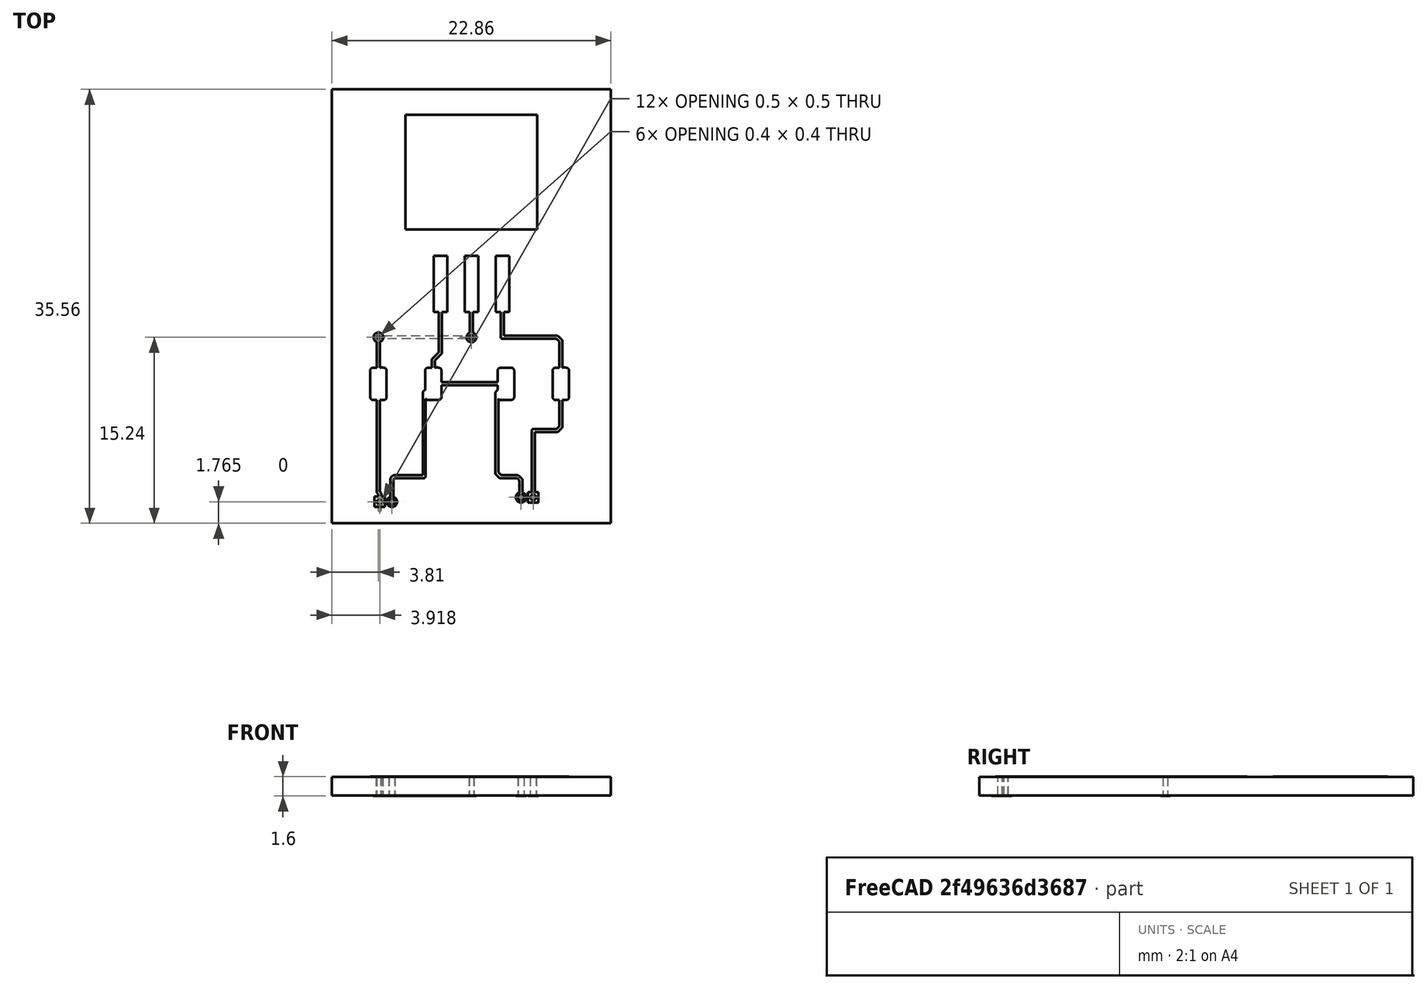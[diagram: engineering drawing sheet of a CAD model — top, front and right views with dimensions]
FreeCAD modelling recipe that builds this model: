
FCSTD DOCUMENT  (FreeCAD 0.18R15221 (Git))
Label: copper
License: All rights reserved
LicenseURL: http://en.wikipedia.org/wiki/All_rights_reserved
objects: Path::FeatureArea×19, Part::Feature×15, Part::Extrusion×5, Part::MultiFuse×1, Part::Cut×1
note: 60 computed .brp shape members not serialized (recipe doc carries the construction recipe); baked Part::Feature solids carry a one-line shape summary decoded from their .brp

FEATURE [Part::Feature] holes_wire  label="holes_wire#F.Cu#0"
  shape: bbox 13.13 x 13.93 x 2e-07 mm, 0 faces, 0 solids (baked)
FEATURE [Part::Feature] board_wire  label="board_wire#F.Cu"
  shape: bbox 22.86 x 35.56 x 2e-07 mm, 0 faces, 0 solids (baked)
FEATURE [Path::FeatureArea] board_area  label="board_area#F.Cu"
  Accuracy = 0.01
  Angle = 45
  AngleShift = 0
  CleanDistance = 0
  ClipFill = 0
  ClipperScale = 10000000
  Coplanar = 0
  Deflection = 0.01
  EndType = 0
  Explode = false
  ExtraPass = 0
  Fill = 1
  FitArcs = false
  FromCenter = false
  JoinType = 0
  LastStepover = 0
  MaxArcPoints = 100
  MinArcPoints = 4
  MiterLimit = 2
  OpenMode = 0
  Operation = 0
  Outline = false
  PocketExtraOffset = 0
  PocketLastStepover = 0
  PocketMode = 0
  PocketStepover = 0
  Project = false
  Reorient = false
  RoundPrecision = 0
  SectionCount = 0
  SectionMode = 2
  SectionOffset = 0
  SectionTolerance = 1e-06
  Shift = 0
  Simplify = false
  Sources = -> [board_wire]
  Stepdown = 1
  Stepover = 0
  SubjectFill = 0
  Thicken = false
  Tolerance = 1e-07
  ToolRadius = 1
  Unit = 1
FEATURE [Path::FeatureArea] board_area001  label="board_area001#F.Cu"
  Accuracy = 0.01
  Angle = 45
  AngleShift = 0
  CleanDistance = 0
  ClipFill = 0
  ClipperScale = 10000000
  Coplanar = 0
  Deflection = 0.01
  EndType = 0
  Explode = false
  ExtraPass = 0
  Fill = 1
  FitArcs = true
  FromCenter = false
  JoinType = 0
  LastStepover = 0
  MaxArcPoints = 100
  MinArcPoints = 4
  MiterLimit = 2
  OpenMode = 0
  Operation = 1
  Outline = false
  PocketExtraOffset = 0
  PocketLastStepover = 0
  PocketMode = 0
  PocketStepover = 0
  Project = false
  Reorient = false
  RoundPrecision = 0
  SectionCount = 0
  SectionMode = 2
  SectionOffset = 0
  SectionTolerance = 1e-06
  Shift = 0
  Simplify = false
  Sources = -> [board_area,holes_wire]
  Stepdown = 1
  Stepover = 0
  SubjectFill = 0
  Thicken = false
  Tolerance = 1e-07
  ToolRadius = 1
  Unit = 1
FEATURE [Part::Extrusion] board_solid  label="board_solid#F.Cu"
  Base = -> board_area001
  Dir = (0,0,1.53)
  DirMode = 0
  FaceMakerClass = Part::FaceMakerBullseye
  LengthFwd = 0
  LengthRev = 0
  Solid = false
  Symmetric = false
FEATURE [Part::Feature] pads_wire  label="pads_wire#F.Cu#0#C2"
  shape: bbox 5.85 x 2.65 x 2e-07 mm, 0 faces, 0 solids (baked)
FEATURE [Path::FeatureArea] pads_area  label="pads_area#F.Cu#0#C2"
  Accuracy = 0.01
  Angle = 45
  AngleShift = 0
  CleanDistance = 0
  ClipFill = 0
  ClipperScale = 10000000
  Coplanar = 0
  Deflection = 0.01
  EndType = 0
  Explode = false
  ExtraPass = 0
  Fill = 1
  FitArcs = false
  FromCenter = false
  JoinType = 0
  LastStepover = 0
  MaxArcPoints = 100
  MinArcPoints = 4
  MiterLimit = 2
  OpenMode = 0
  Operation = 0
  Outline = false
  Placement = pos=(199.1,-80.01,0) rot=(0,0,1;0rad)
  PocketExtraOffset = 0
  PocketLastStepover = 0
  PocketMode = 0
  PocketStepover = 0
  Project = false
  Reorient = false
  RoundPrecision = 0
  SectionCount = 0
  SectionMode = 2
  SectionOffset = 0
  SectionTolerance = 1e-06
  Shift = 0
  Simplify = false
  Sources = -> [pads_wire]
  Stepdown = 1
  Stepover = 0
  SubjectFill = 0
  Thicken = false
  Tolerance = 1e-07
  ToolRadius = 1
  Unit = 1
FEATURE [Part::Feature] pads_wire001  label="pads_wire001#F.Cu#1#J2"
  shape: bbox 0.85 x 1.85 x 2e-07 mm, 0 faces, 0 solids (baked)
FEATURE [Path::FeatureArea] pads_area001  label="pads_area001#F.Cu#1#J2"
  Accuracy = 0.01
  Angle = 45
  AngleShift = 0
  CleanDistance = 0
  ClipFill = 0
  ClipperScale = 10000000
  Coplanar = 0
  Deflection = 0.01
  EndType = 0
  Explode = false
  ExtraPass = 0
  Fill = 1
  FitArcs = false
  FromCenter = false
  JoinType = 0
  LastStepover = 0
  MaxArcPoints = 100
  MinArcPoints = 4
  MiterLimit = 2
  OpenMode = 0
  Operation = 0
  Outline = false
  Placement = pos=(196.958,-89.6755,0) rot=(0,0,1;1.5708rad)
  PocketExtraOffset = 0
  PocketLastStepover = 0
  PocketMode = 0
  PocketStepover = 0
  Project = false
  Reorient = false
  RoundPrecision = 0
  SectionCount = 0
  SectionMode = 2
  SectionOffset = 0
  SectionTolerance = 1e-06
  Shift = 0
  Simplify = false
  Sources = -> [pads_wire001]
  Stepdown = 1
  Stepover = 0
  SubjectFill = 0
  Thicken = false
  Tolerance = 1e-07
  ToolRadius = 1
  Unit = 1
FEATURE [Part::Feature] pads_wire002  label="pads_wire002#F.Cu#2#J1"
  shape: bbox 0.85 x 1.85 x 2e-07 mm, 0 faces, 0 solids (baked)
FEATURE [Path::FeatureArea] pads_area002  label="pads_area002#F.Cu#2#J1"
  Accuracy = 0.01
  Angle = 45
  AngleShift = 0
  CleanDistance = 0
  ClipFill = 0
  ClipperScale = 10000000
  Coplanar = 0
  Deflection = 0.01
  EndType = 0
  Explode = false
  ExtraPass = 0
  Fill = 1
  FitArcs = false
  FromCenter = false
  JoinType = 0
  LastStepover = 0
  MaxArcPoints = 100
  MinArcPoints = 4
  MiterLimit = 2
  OpenMode = 0
  Operation = 0
  Outline = false
  Placement = pos=(209.534,-89.3136,0) rot=(0,0,1;4.71239rad)
  PocketExtraOffset = 0
  PocketLastStepover = 0
  PocketMode = 0
  PocketStepover = 0
  Project = false
  Reorient = false
  RoundPrecision = 0
  SectionCount = 0
  SectionMode = 2
  SectionOffset = 0
  SectionTolerance = 1e-06
  Shift = 0
  Simplify = false
  Sources = -> [pads_wire002]
  Stepdown = 1
  Stepover = 0
  SubjectFill = 0
  Thicken = false
  Tolerance = 1e-07
  ToolRadius = 1
  Unit = 1
FEATURE [Part::Feature] pads_wire003  label="pads_wire003#F.Cu#3#C1"
  shape: bbox 5.85 x 2.65 x 2e-07 mm, 0 faces, 0 solids (baked)
FEATURE [Path::FeatureArea] pads_area003  label="pads_area003#F.Cu#3#C1"
  Accuracy = 0.01
  Angle = 45
  AngleShift = 0
  CleanDistance = 0
  ClipFill = 0
  ClipperScale = 10000000
  Coplanar = 0
  Deflection = 0.01
  EndType = 0
  Explode = false
  ExtraPass = 0
  Fill = 1
  FitArcs = false
  FromCenter = false
  JoinType = 0
  LastStepover = 0
  MaxArcPoints = 100
  MinArcPoints = 4
  MiterLimit = 2
  OpenMode = 0
  Operation = 0
  Outline = false
  Placement = pos=(209.55,-80.01,0) rot=(0,0,1;3.14159rad)
  PocketExtraOffset = 0
  PocketLastStepover = 0
  PocketMode = 0
  PocketStepover = 0
  Project = false
  Reorient = false
  RoundPrecision = 0
  SectionCount = 0
  SectionMode = 2
  SectionOffset = 0
  SectionTolerance = 1e-06
  Shift = 0
  Simplify = false
  Sources = -> [pads_wire003]
  Stepdown = 1
  Stepover = 0
  SubjectFill = 0
  Thicken = false
  Tolerance = 1e-07
  ToolRadius = 1
  Unit = 1
FEATURE [Part::Feature] pads_wire004  label="pads_wire004#F.Cu#4#U1"
  shape: bbox 16.15 x 10.8 x 2e-07 mm, 0 faces, 0 solids (baked)
FEATURE [Path::FeatureArea] pads_area004  label="pads_area004#F.Cu#4#U1"
  Accuracy = 0.01
  Angle = 45
  AngleShift = 0
  CleanDistance = 0
  ClipFill = 0
  ClipperScale = 10000000
  Coplanar = 0
  Deflection = 0.01
  EndType = 0
  Explode = false
  ExtraPass = 0
  Fill = 1
  FitArcs = false
  FromCenter = false
  JoinType = 0
  LastStepover = 0
  MaxArcPoints = 100
  MinArcPoints = 4
  MiterLimit = 2
  OpenMode = 0
  Operation = 0
  Outline = false
  Placement = pos=(204.47,-66.04,0) rot=(0,0,1;1.5708rad)
  PocketExtraOffset = 0
  PocketLastStepover = 0
  PocketMode = 0
  PocketStepover = 0
  Project = false
  Reorient = false
  RoundPrecision = 0
  SectionCount = 0
  SectionMode = 2
  SectionOffset = 0
  SectionTolerance = 1e-06
  Shift = 0
  Simplify = false
  Sources = -> [pads_wire004]
  Stepdown = 1
  Stepover = 0
  SubjectFill = 0
  Thicken = false
  Tolerance = 1e-07
  ToolRadius = 1
  Unit = 1
FEATURE [Part::Feature] vias_wire  label="vias_wire#F.Cu"
  shape: bbox 8.42 x 0.8 x 2e-07 mm, 0 faces, 0 solids (baked)
FEATURE [Path::FeatureArea] vias_area  label="vias_area#F.Cu"
  Accuracy = 0.01
  Angle = 45
  AngleShift = 0
  CleanDistance = 0
  ClipFill = 0
  ClipperScale = 10000000
  Coplanar = 0
  Deflection = 0.01
  EndType = 0
  Explode = false
  ExtraPass = 0
  Fill = 1
  FitArcs = false
  FromCenter = false
  JoinType = 0
  LastStepover = 0
  MaxArcPoints = 100
  MinArcPoints = 4
  MiterLimit = 2
  OpenMode = 0
  Operation = 0
  Outline = false
  PocketExtraOffset = 0
  PocketLastStepover = 0
  PocketMode = 0
  PocketStepover = 0
  Project = false
  Reorient = false
  RoundPrecision = 0
  SectionCount = 0
  SectionMode = 2
  SectionOffset = 0
  SectionTolerance = 1e-06
  Shift = 0
  Simplify = false
  Sources = -> [vias_wire]
  Stepdown = 1
  Stepover = 0
  SubjectFill = 0
  Thicken = false
  Tolerance = 1e-07
  ToolRadius = 1
  Unit = 1
FEATURE [Path::FeatureArea] pads_area005  label="pads_area005#F.Cu"
  Accuracy = 0.01
  Angle = 45
  AngleShift = 0
  CleanDistance = 0
  ClipFill = 0
  ClipperScale = 10000000
  Coplanar = 0
  Deflection = 0.01
  EndType = 0
  Explode = false
  ExtraPass = 0
  Fill = 2
  FitArcs = true
  FromCenter = false
  JoinType = 0
  LastStepover = 0
  MaxArcPoints = 100
  MinArcPoints = 4
  MiterLimit = 2
  OpenMode = 0
  Operation = 0
  Outline = false
  PocketExtraOffset = 0
  PocketLastStepover = 0
  PocketMode = 0
  PocketStepover = 0
  Project = false
  Reorient = false
  RoundPrecision = 0
  SectionCount = 0
  SectionMode = 2
  SectionOffset = 0
  SectionTolerance = 1e-06
  Shift = 0
  Simplify = false
  Sources = -> [pads_area,pads_area001,pads_area002,pads_area003,pads_area004,vias_area]
  Stepdown = 1
  Stepover = 0
  SubjectFill = 0
  Thicken = false
  Tolerance = 1e-07
  ToolRadius = 1
  Unit = 1
FEATURE [Part::Feature] track_wire  label="track_wire#F.Cu#0.25"
  shape: bbox 14.95 x 17.86 x 2e-07 mm, 0 faces, 0 solids (baked)
FEATURE [Path::FeatureArea] track_area  label="track_area#F.Cu#0.25"
  Accuracy = 0.01
  Angle = 45
  AngleShift = 0
  CleanDistance = 0
  ClipFill = 0
  ClipperScale = 10000000
  Coplanar = 0
  Deflection = 0.01
  EndType = 0
  Explode = false
  ExtraPass = 0
  Fill = 1
  FitArcs = false
  FromCenter = false
  JoinType = 0
  LastStepover = 0
  MaxArcPoints = 100
  MinArcPoints = 4
  MiterLimit = 2
  Offset = 0.125
  OpenMode = 0
  Operation = 0
  Outline = false
  PocketExtraOffset = 0
  PocketLastStepover = 0
  PocketMode = 0
  PocketStepover = 0
  Project = false
  Reorient = false
  RoundPrecision = 0
  SectionCount = 0
  SectionMode = 2
  SectionOffset = 0
  SectionTolerance = 1e-06
  Shift = 0
  Simplify = false
  Sources = -> [track_wire]
  Stepdown = 1
  Stepover = 0
  SubjectFill = 0
  Thicken = false
  Tolerance = 1e-07
  ToolRadius = 1
  Unit = 1
FEATURE [Path::FeatureArea] copper_area  label="copper_area#F.Cu"
  Accuracy = 0.01
  Angle = 45
  AngleShift = 0
  CleanDistance = 0
  ClipFill = 0
  ClipperScale = 10000000
  Coplanar = 0
  Deflection = 0.01
  EndType = 0
  Explode = false
  ExtraPass = 0
  Fill = 2
  FitArcs = true
  FromCenter = false
  JoinType = 0
  LastStepover = 0
  MaxArcPoints = 100
  MinArcPoints = 4
  MiterLimit = 2
  OpenMode = 0
  Operation = 0
  Outline = false
  PocketExtraOffset = 0
  PocketLastStepover = 0
  PocketMode = 0
  PocketStepover = 0
  Project = false
  Reorient = false
  RoundPrecision = 0
  SectionCount = 0
  SectionMode = 2
  SectionOffset = 0
  SectionTolerance = 1e-06
  Shift = 0
  Simplify = false
  Sources = -> [pads_area005,track_area]
  Stepdown = 1
  Stepover = 0
  SubjectFill = 0
  Thicken = false
  Tolerance = 1e-07
  ToolRadius = 1
  Unit = 1
FEATURE [Part::Extrusion] copper_solid  label="copper_solid#F.Cu"
  Base = -> copper_area
  Dir = (0,0,0.035)
  DirMode = 0
  FaceMakerClass = Part::FaceMakerBullseye
  LengthFwd = 0
  LengthRev = 0
  Placement = pos=(0,0,1.53) rot=(0,0,1;0rad)
  Solid = false
  Symmetric = false
FEATURE [Part::Feature] pads_wire005  label="pads_wire005#B.Cu#1#J2"
  shape: bbox 0.85 x 1.85 x 2e-07 mm, 0 faces, 0 solids (baked)
FEATURE [Path::FeatureArea] pads_area006  label="pads_area006#B.Cu#1#J2"
  Accuracy = 0.01
  Angle = 45
  AngleShift = 0
  CleanDistance = 0
  ClipFill = 0
  ClipperScale = 10000000
  Coplanar = 0
  Deflection = 0.01
  EndType = 0
  Explode = false
  ExtraPass = 0
  Fill = 1
  FitArcs = false
  FromCenter = false
  JoinType = 0
  LastStepover = 0
  MaxArcPoints = 100
  MinArcPoints = 4
  MiterLimit = 2
  OpenMode = 0
  Operation = 0
  Outline = false
  Placement = pos=(196.958,-89.6755,0) rot=(0,0,1;1.5708rad)
  PocketExtraOffset = 0
  PocketLastStepover = 0
  PocketMode = 0
  PocketStepover = 0
  Project = false
  Reorient = false
  RoundPrecision = 0
  SectionCount = 0
  SectionMode = 2
  SectionOffset = 0
  SectionTolerance = 1e-06
  Shift = 0
  Simplify = false
  Sources = -> [pads_wire005]
  Stepdown = 1
  Stepover = 0
  SubjectFill = 0
  Thicken = false
  Tolerance = 1e-07
  ToolRadius = 1
  Unit = 1
FEATURE [Part::Feature] pads_wire006  label="pads_wire006#B.Cu#2#J1"
  shape: bbox 0.85 x 1.85 x 2e-07 mm, 0 faces, 0 solids (baked)
FEATURE [Path::FeatureArea] pads_area007  label="pads_area007#B.Cu#2#J1"
  Accuracy = 0.01
  Angle = 45
  AngleShift = 0
  CleanDistance = 0
  ClipFill = 0
  ClipperScale = 10000000
  Coplanar = 0
  Deflection = 0.01
  EndType = 0
  Explode = false
  ExtraPass = 0
  Fill = 1
  FitArcs = false
  FromCenter = false
  JoinType = 0
  LastStepover = 0
  MaxArcPoints = 100
  MinArcPoints = 4
  MiterLimit = 2
  OpenMode = 0
  Operation = 0
  Outline = false
  Placement = pos=(209.534,-89.3136,0) rot=(0,0,1;4.71239rad)
  PocketExtraOffset = 0
  PocketLastStepover = 0
  PocketMode = 0
  PocketStepover = 0
  Project = false
  Reorient = false
  RoundPrecision = 0
  SectionCount = 0
  SectionMode = 2
  SectionOffset = 0
  SectionTolerance = 1e-06
  Shift = 0
  Simplify = false
  Sources = -> [pads_wire006]
  Stepdown = 1
  Stepover = 0
  SubjectFill = 0
  Thicken = false
  Tolerance = 1e-07
  ToolRadius = 1
  Unit = 1
FEATURE [Part::Feature] vias_wire001  label="vias_wire001#B.Cu"
  shape: bbox 8.42 x 0.8 x 2e-07 mm, 0 faces, 0 solids (baked)
FEATURE [Path::FeatureArea] vias_area001  label="vias_area001#B.Cu"
  Accuracy = 0.01
  Angle = 45
  AngleShift = 0
  CleanDistance = 0
  ClipFill = 0
  ClipperScale = 10000000
  Coplanar = 0
  Deflection = 0.01
  EndType = 0
  Explode = false
  ExtraPass = 0
  Fill = 1
  FitArcs = false
  FromCenter = false
  JoinType = 0
  LastStepover = 0
  MaxArcPoints = 100
  MinArcPoints = 4
  MiterLimit = 2
  OpenMode = 0
  Operation = 0
  Outline = false
  PocketExtraOffset = 0
  PocketLastStepover = 0
  PocketMode = 0
  PocketStepover = 0
  Project = false
  Reorient = false
  RoundPrecision = 0
  SectionCount = 0
  SectionMode = 2
  SectionOffset = 0
  SectionTolerance = 1e-06
  Shift = 0
  Simplify = false
  Sources = -> [vias_wire001]
  Stepdown = 1
  Stepover = 0
  SubjectFill = 0
  Thicken = false
  Tolerance = 1e-07
  ToolRadius = 1
  Unit = 1
FEATURE [Path::FeatureArea] pads_area008  label="pads_area008#B.Cu"
  Accuracy = 0.01
  Angle = 45
  AngleShift = 0
  CleanDistance = 0
  ClipFill = 0
  ClipperScale = 10000000
  Coplanar = 0
  Deflection = 0.01
  EndType = 0
  Explode = false
  ExtraPass = 0
  Fill = 2
  FitArcs = true
  FromCenter = false
  JoinType = 0
  LastStepover = 0
  MaxArcPoints = 100
  MinArcPoints = 4
  MiterLimit = 2
  OpenMode = 0
  Operation = 0
  Outline = false
  PocketExtraOffset = 0
  PocketLastStepover = 0
  PocketMode = 0
  PocketStepover = 0
  Project = false
  Reorient = false
  RoundPrecision = 0
  SectionCount = 0
  SectionMode = 2
  SectionOffset = 0
  SectionTolerance = 1e-06
  Shift = 0
  Simplify = false
  Sources = -> [pads_area006,pads_area007,vias_area001]
  Stepdown = 1
  Stepover = 0
  SubjectFill = 0
  Thicken = false
  Tolerance = 1e-07
  ToolRadius = 1
  Unit = 1
FEATURE [Part::Feature] track_wire001  label="track_wire001#B.Cu#0.25"
  shape: bbox 7.62 x 14.15 x 2e-07 mm, 0 faces, 0 solids (baked)
FEATURE [Path::FeatureArea] track_area001  label="track_area001#B.Cu#0.25"
  Accuracy = 0.01
  Angle = 45
  AngleShift = 0
  CleanDistance = 0
  ClipFill = 0
  ClipperScale = 10000000
  Coplanar = 0
  Deflection = 0.01
  EndType = 0
  Explode = false
  ExtraPass = 0
  Fill = 1
  FitArcs = false
  FromCenter = false
  JoinType = 0
  LastStepover = 0
  MaxArcPoints = 100
  MinArcPoints = 4
  MiterLimit = 2
  Offset = 0.125
  OpenMode = 0
  Operation = 0
  Outline = false
  PocketExtraOffset = 0
  PocketLastStepover = 0
  PocketMode = 0
  PocketStepover = 0
  Project = false
  Reorient = false
  RoundPrecision = 0
  SectionCount = 0
  SectionMode = 2
  SectionOffset = 0
  SectionTolerance = 1e-06
  Shift = 0
  Simplify = false
  Sources = -> [track_wire001]
  Stepdown = 1
  Stepover = 0
  SubjectFill = 0
  Thicken = false
  Tolerance = 1e-07
  ToolRadius = 1
  Unit = 1
FEATURE [Path::FeatureArea] copper_area001  label="copper_area001#B.Cu"
  Accuracy = 0.01
  Angle = 45
  AngleShift = 0
  CleanDistance = 0
  ClipFill = 0
  ClipperScale = 10000000
  Coplanar = 0
  Deflection = 0.01
  EndType = 0
  Explode = false
  ExtraPass = 0
  Fill = 2
  FitArcs = true
  FromCenter = false
  JoinType = 0
  LastStepover = 0
  MaxArcPoints = 100
  MinArcPoints = 4
  MiterLimit = 2
  OpenMode = 0
  Operation = 0
  Outline = false
  PocketExtraOffset = 0
  PocketLastStepover = 0
  PocketMode = 0
  PocketStepover = 0
  Project = false
  Reorient = false
  RoundPrecision = 0
  SectionCount = 0
  SectionMode = 2
  SectionOffset = 0
  SectionTolerance = 1e-06
  Shift = 0
  Simplify = false
  Sources = -> [pads_area008,track_area001]
  Stepdown = 1
  Stepover = 0
  SubjectFill = 0
  Thicken = false
  Tolerance = 1e-07
  ToolRadius = 1
  Unit = 1
FEATURE [Part::Extrusion] copper_solid001  label="copper_solid001#B.Cu"
  Base = -> copper_area001
  Dir = (0,0,0.035)
  DirMode = 0
  FaceMakerClass = Part::FaceMakerBullseye
  LengthFwd = 0
  LengthRev = 0
  Placement = pos=(0,0,-0.035) rot=(0,0,1;0rad)
  Solid = false
  Symmetric = false
FEATURE [Part::Feature] holes_wire001  label="holes_wire001#F.Cu#0"
  shape: bbox 13.13 x 13.93 x 2e-07 mm, 0 faces, 0 solids (baked)
FEATURE [Path::FeatureArea] holes_area  label="holes_area#F.Cu#0"
  Accuracy = 0.01
  Angle = 45
  AngleShift = 0
  CleanDistance = 0
  ClipFill = 0
  ClipperScale = 10000000
  Coplanar = 0
  Deflection = 0.01
  EndType = 0
  Explode = false
  ExtraPass = 0
  Fill = 1
  FitArcs = true
  FromCenter = false
  JoinType = 0
  LastStepover = 0
  MaxArcPoints = 100
  MinArcPoints = 4
  MiterLimit = 2
  OpenMode = 0
  Operation = 0
  Outline = false
  PocketExtraOffset = 0
  PocketLastStepover = 0
  PocketMode = 0
  PocketStepover = 0
  Project = false
  Reorient = false
  RoundPrecision = 0
  SectionCount = 0
  SectionMode = 2
  SectionOffset = 0
  SectionTolerance = 1e-06
  Shift = 0
  Simplify = false
  Sources = -> [holes_wire001]
  Stepdown = 1
  Stepover = 0
  SubjectFill = 0
  Thicken = false
  Tolerance = 1e-07
  ToolRadius = 1
  Unit = 1
FEATURE [Part::Extrusion] holes_solid  label="holes_solid#F.Cu#th"
  Base = -> holes_area
  Dir = (0,0,1.565)
  DirMode = 0
  FaceMakerClass = Part::FaceMakerBullseye
  LengthFwd = 0
  LengthRev = 0
  Placement = pos=(0,0,-0.0175) rot=(0,0,1;0rad)
  Solid = false
  Symmetric = false
FEATURE [Part::MultiFuse] coppers_fuse  label="coppers_fuse#F.Cu"
  Shapes = -> [copper_solid,copper_solid001,holes_solid]
FEATURE [Part::Feature] holes_wire002  label="holes_wire002#F.Cu#0"
  shape: bbox 13.1 x 13.89 x 2e-07 mm, 0 faces, 0 solids (baked)
FEATURE [Path::FeatureArea] holes_area001  label="holes_area001#F.Cu#0"
  Accuracy = 0.01
  Angle = 45
  AngleShift = 0
  CleanDistance = 0
  ClipFill = 0
  ClipperScale = 10000000
  Coplanar = 0
  Deflection = 0.01
  EndType = 0
  Explode = false
  ExtraPass = 0
  Fill = 1
  FitArcs = true
  FromCenter = false
  JoinType = 0
  LastStepover = 0
  MaxArcPoints = 100
  MinArcPoints = 4
  MiterLimit = 2
  OpenMode = 0
  Operation = 0
  Outline = false
  PocketExtraOffset = 0
  PocketLastStepover = 0
  PocketMode = 0
  PocketStepover = 0
  Project = false
  Reorient = false
  RoundPrecision = 0
  SectionCount = 0
  SectionMode = 2
  SectionOffset = 0
  SectionTolerance = 1e-06
  Shift = 0
  Simplify = false
  Sources = -> [holes_wire002]
  Stepdown = 1
  Stepover = 0
  SubjectFill = 0
  Thicken = false
  Tolerance = 1e-07
  ToolRadius = 1
  Unit = 1
FEATURE [Part::Extrusion] holes_solid001  label="holes_solid001#F.Cu#th"
  Base = -> holes_area001
  Dir = (0,0,1.74)
  DirMode = 0
  FaceMakerClass = Part::FaceMakerBullseye
  LengthFwd = 0
  LengthRev = 0
  Placement = pos=(0,0,-0.07) rot=(0,0,1;0rad)
  Solid = false
  Symmetric = false
FEATURE [Part::Cut] coppers_drilled  label="coppers_drilled#F.Cu"
  Base = -> coppers_fuse
  Tool = -> holes_solid001
